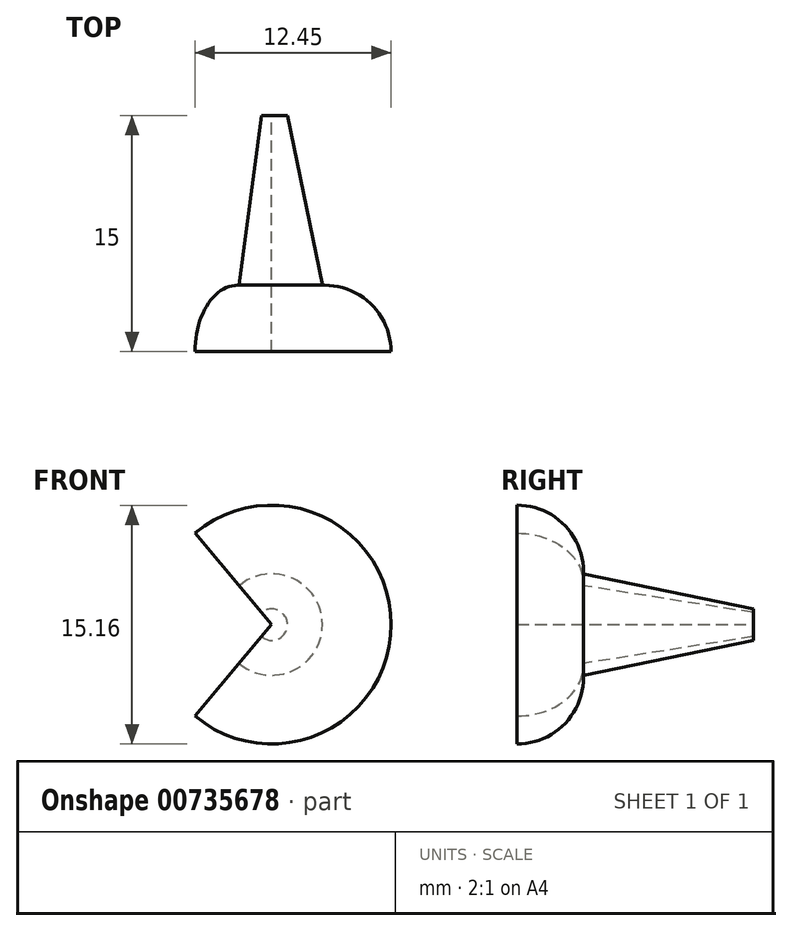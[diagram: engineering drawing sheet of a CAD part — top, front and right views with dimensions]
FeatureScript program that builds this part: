
annotation { "Feature Type Name" : "Feature", "Feature Type Description" : "" }
export const myFeature = defineFeature(function(context is Context, id is Id, definition is map)
    precondition{}
    {
        {
            var Q0;
            Q0=qCreatedBy(makeId("Top.planeOp"),FACE);
            var sketch = newSketch(context, id + "F0", { "sketchPlane" : qUnion([Q0])});
            skLineSegment(sketch, "E0", {"start": v(0, 0) * mm, "end": v(0, 15) * mm});
            skLineSegment(sketch, "E1", {"start": v(1, 15) * mm, "end": v(3.22, 4.23) * mm});
            skArc(sketch, "E2", {"start": v(7.58, 0) * mm, "mid": v(6.3, 3.04) * mm, "end": v(3.22, 4.23) * mm});
            skLineSegment(sketch, "E3", {"start": v(0.5, 15) * mm, "end": v(0.5, 0) * mm});
            skLineSegment(sketch, "E4", {"start": v(0, 0) * mm, "end": v(7.58, 0) * mm});
            skLineSegment(sketch, "E5", {"start": v(0, 15) * mm, "end": v(1, 15) * mm});
            skSolve(sketch);
        }
        {
            var Q0;
            Q0 = qSketchRegion(id + "F0", true);
            var Q1;
            Q1=sQuery(id+"F0.wireOp",EDGE,"E0");
            revolve(context, id + "F1", {"surfaceOperationType" : NewSurfaceOperationType.NEW, "entities" : qUnion([Q0]), "axis" : qUnion([Q1]), "revolveType" : RevolveType.SYMMETRIC, "oppositeDirection" : true, "angle" : 260 * degree});
        }
    });
